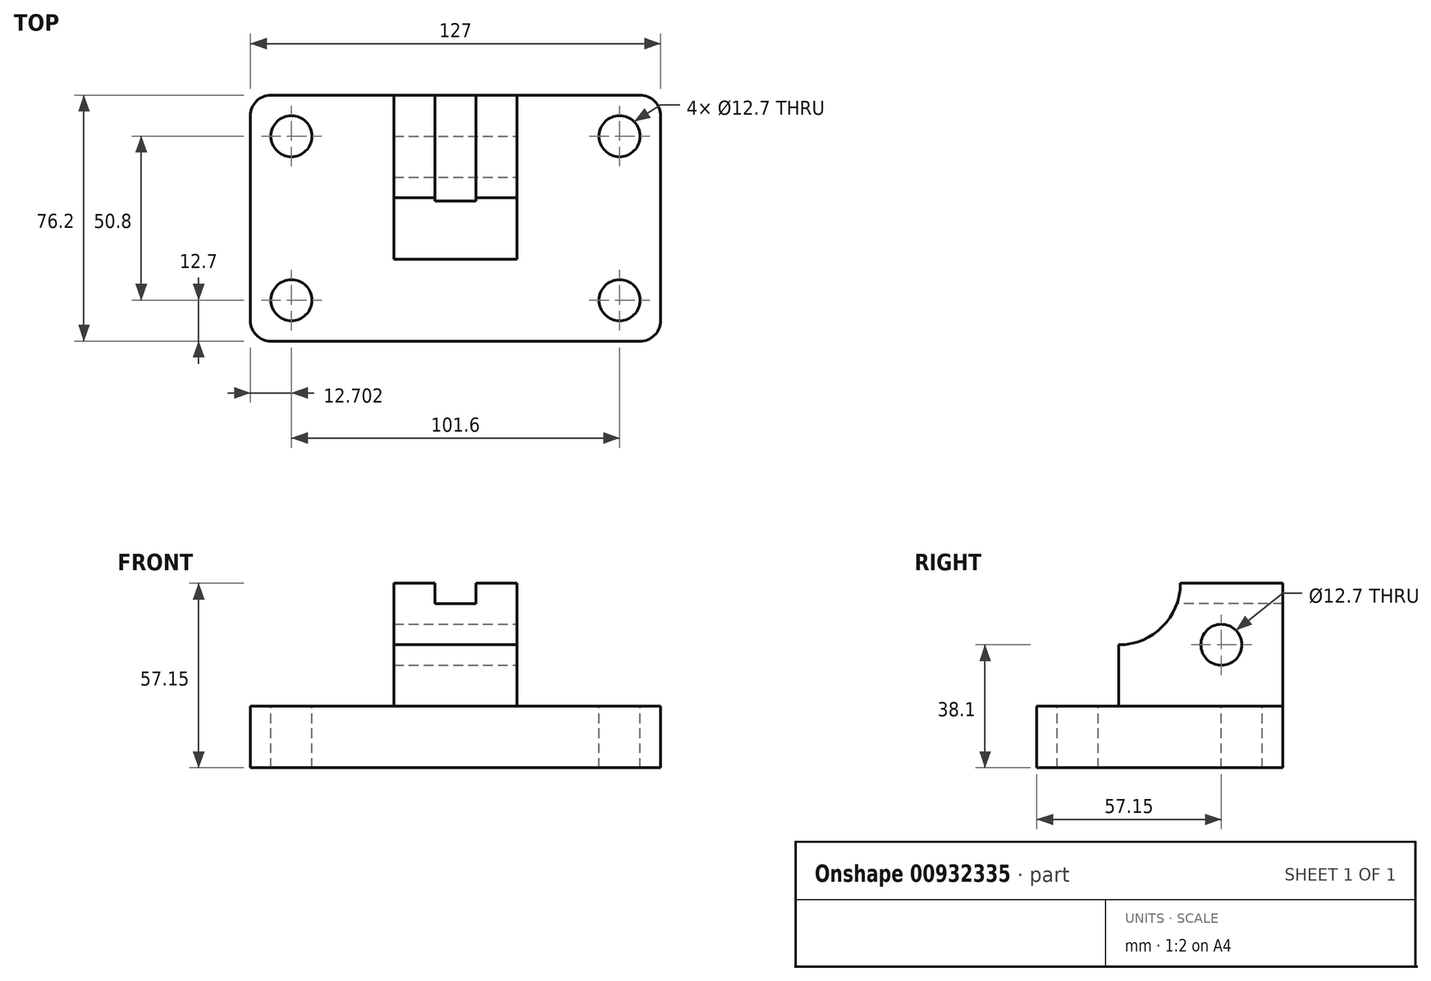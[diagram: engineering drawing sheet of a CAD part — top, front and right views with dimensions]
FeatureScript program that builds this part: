
annotation { "Feature Type Name" : "Feature", "Feature Type Description" : "" }
export const myFeature = defineFeature(function(context is Context, id is Id, definition is map)
    precondition{}
    {
        {
            var Q0;
            Q0=qCreatedBy(makeId("Top.planeOp"),FACE);
            var sketch = newSketch(context, id + "F0", { "sketchPlane" : qUnion([Q0])});
            skLineSegment(sketch, "E0.bottom", {"start": v(-41.85, 38.25) * mm, "end": v(85.15, 38.25) * mm});
            skLineSegment(sketch, "E0.top", {"start": v(-41.85, -37.95) * mm, "end": v(85.15, -37.95) * mm});
            skLineSegment(sketch, "E0.left", {"start": v(-41.85, 38.25) * mm, "end": v(-41.85, -37.95) * mm});
            skLineSegment(sketch, "E0.right", {"start": v(85.15, 38.25) * mm, "end": v(85.15, -37.95) * mm});
            skCircle(sketch, "E1", {"center": v(-29.15, 25.55) * mm, "radius": 6.35 * mm});
            skCircle(sketch, "E2", {"center": v(72.45, 25.55) * mm, "radius": 6.35 * mm});
            skCircle(sketch, "E3", {"center": v(-29.15, -25.25) * mm, "radius": 6.35 * mm});
            skCircle(sketch, "E4", {"center": v(72.45, -25.25) * mm, "radius": 6.35 * mm});
            skSolve(sketch);
        }
        {
            var Q0;
            Q0 = qSketchRegion(id + "F0", true);
            extrude(context, id + "F1", {"entities" : qUnion([Q0]), "oppositeDirection" : true, "depth" : 19.05 * mm, "offsetDistance" : 25.4 * mm});
        }
        {
            var Q0;
            Q0=makeQuery(id+"F1.opExtrude","CAP_FACE",FACE,{"disambiguationData":[OSD([sQuery(id+"F0.wireOp",EDGE,"E0.bottom"),sQuery(id+"F0.wireOp",EDGE,"E0.top"),sQuery(id+"F0.wireOp",EDGE,"E0.left"),sQuery(id+"F0.wireOp",EDGE,"E0.right"),sQuery(id+"F0.wireOp",EDGE,"E1"),sQuery(id+"F0.wireOp",EDGE,"E2"),sQuery(id+"F0.wireOp",EDGE,"E3"),sQuery(id+"F0.wireOp",EDGE,"E4")])],"isStart":true});
            var sketch = newSketch(context, id + "F2", { "sketchPlane" : qUnion([Q0])});
            skLineSegment(sketch, "E5.bottom", {"start": v(2.6, 38.25) * mm, "end": v(40.7, 38.25) * mm});
            skLineSegment(sketch, "E5.top", {"start": v(2.6, -12.55) * mm, "end": v(40.7, -12.55) * mm});
            skLineSegment(sketch, "E5.left", {"start": v(2.6, 38.25) * mm, "end": v(2.6, -12.55) * mm});
            skLineSegment(sketch, "E5.right", {"start": v(40.7, 38.25) * mm, "end": v(40.7, -12.55) * mm});
            skSolve(sketch);
        }
        {
            var Q0;
            Q0 = qSketchRegion(id + "F2", true);
            extrude(context, id + "F3", {"entities" : qUnion([Q0]), "operationType" : NewBodyOperationType.ADD, "depth" : 38.1 * mm, "offsetDistance" : 25.4 * mm});
        }
        {
            var Q0;
            Q0=makeQuery(id+"F3.opExtrude","SWEPT_FACE",FACE,{"disambiguationData":[OSD([sQuery(id+"F2.wireOp",EDGE,"E5.right")])]});
            var sketch = newSketch(context, id + "F4", { "sketchPlane" : qUnion([Q0])});
            skCircle(sketch, "E6", {"center": v(-12.55, 38.1) * mm, "radius": 19.05 * mm});
            skSolve(sketch);
        }
        {
            var Q0;
            Q0 = qSketchRegion(id + "F4", true);
            extrude(context, id + "F5", {"entities" : qUnion([Q0]), "operationType" : NewBodyOperationType.REMOVE, "endBound" : BoundingType.THROUGH_ALL, "oppositeDirection" : true, "depth" : 25.4 * mm, "offsetDistance" : 25.4 * mm});
        }
        {
            var Q0;
            Q0=makeQuery(id+"F3.opExtrude","CAP_FACE",FACE,{"disambiguationData":[OSD([sQuery(id+"F2.wireOp",EDGE,"E5.bottom"),sQuery(id+"F2.wireOp",EDGE,"E5.top"),sQuery(id+"F2.wireOp",EDGE,"E5.left"),sQuery(id+"F2.wireOp",EDGE,"E5.right")])],"isStart":false});
            var sketch = newSketch(context, id + "F6", { "sketchPlane" : qUnion([Q0])});
            skLineSegment(sketch, "E7.bottom", {"start": v(15.3, 38.25) * mm, "end": v(28, 38.25) * mm});
            skLineSegment(sketch, "E7.top", {"start": v(15.3, 0) * mm, "end": v(28, 0) * mm});
            skLineSegment(sketch, "E7.left", {"start": v(15.3, 38.25) * mm, "end": v(15.3, 0) * mm});
            skLineSegment(sketch, "E7.right", {"start": v(28, 38.25) * mm, "end": v(28, 0) * mm});
            skSolve(sketch);
        }
        {
            var Q0;
            Q0 = qSketchRegion(id + "F6", true);
            extrude(context, id + "F7", {"entities" : qUnion([Q0]), "operationType" : NewBodyOperationType.REMOVE, "oppositeDirection" : true, "depth" : 6.35 * mm, "offsetDistance" : 25.4 * mm});
        }
        {
            var Q0;
            Q0=makeQuery(id+"F3.opExtrude","SWEPT_FACE",FACE,{"disambiguationData":[OSD([sQuery(id+"F2.wireOp",EDGE,"E5.right")])]});
            var sketch = newSketch(context, id + "F8", { "sketchPlane" : qUnion([Q0])});
            skCircle(sketch, "E8", {"center": v(19.2, 19.05) * mm, "radius": 6.35 * mm});
            skSolve(sketch);
        }
        {
            var Q0;
            Q0 = qSketchRegion(id + "F8", true);
            extrude(context, id + "F9", {"entities" : qUnion([Q0]), "operationType" : NewBodyOperationType.REMOVE, "endBound" : BoundingType.THROUGH_ALL, "oppositeDirection" : true, "depth" : 25.4 * mm, "offsetDistance" : 25.4 * mm});
        }
        {
            var Q0;
            Q0=makeQuery(id+"F1.opExtrude","SWEPT_EDGE",EDGE,{"disambiguationData":[OSD([sQuery(id+"F0.wireOp",EDGE,"E0.top"),sQuery(id+"F0.wireOp",EDGE,"E0.left")])]});
            var Q1;
            Q1=makeQuery(id+"F1.opExtrude","SWEPT_EDGE",EDGE,{"disambiguationData":[OSD([sQuery(id+"F0.wireOp",EDGE,"E0.bottom"),sQuery(id+"F0.wireOp",EDGE,"E0.left")])]});
            var Q2;
            Q2=makeQuery(id+"F1.opExtrude","SWEPT_EDGE",EDGE,{"disambiguationData":[OSD([sQuery(id+"F0.wireOp",EDGE,"E0.top"),sQuery(id+"F0.wireOp",EDGE,"E0.right")])]});
            var Q3;
            Q3=makeQuery(id+"F1.opExtrude","SWEPT_EDGE",EDGE,{"disambiguationData":[OSD([sQuery(id+"F0.wireOp",EDGE,"E0.bottom"),sQuery(id+"F0.wireOp",EDGE,"E0.right")])]});
            fillet(context, id + "F10", {"entities" : qUnion([Q0, Q1, Q2, Q3]), "radius" : 6.35 * mm, "tangentPropagation" : true, "allowEdgeOverflow" : false});
        }
    });
